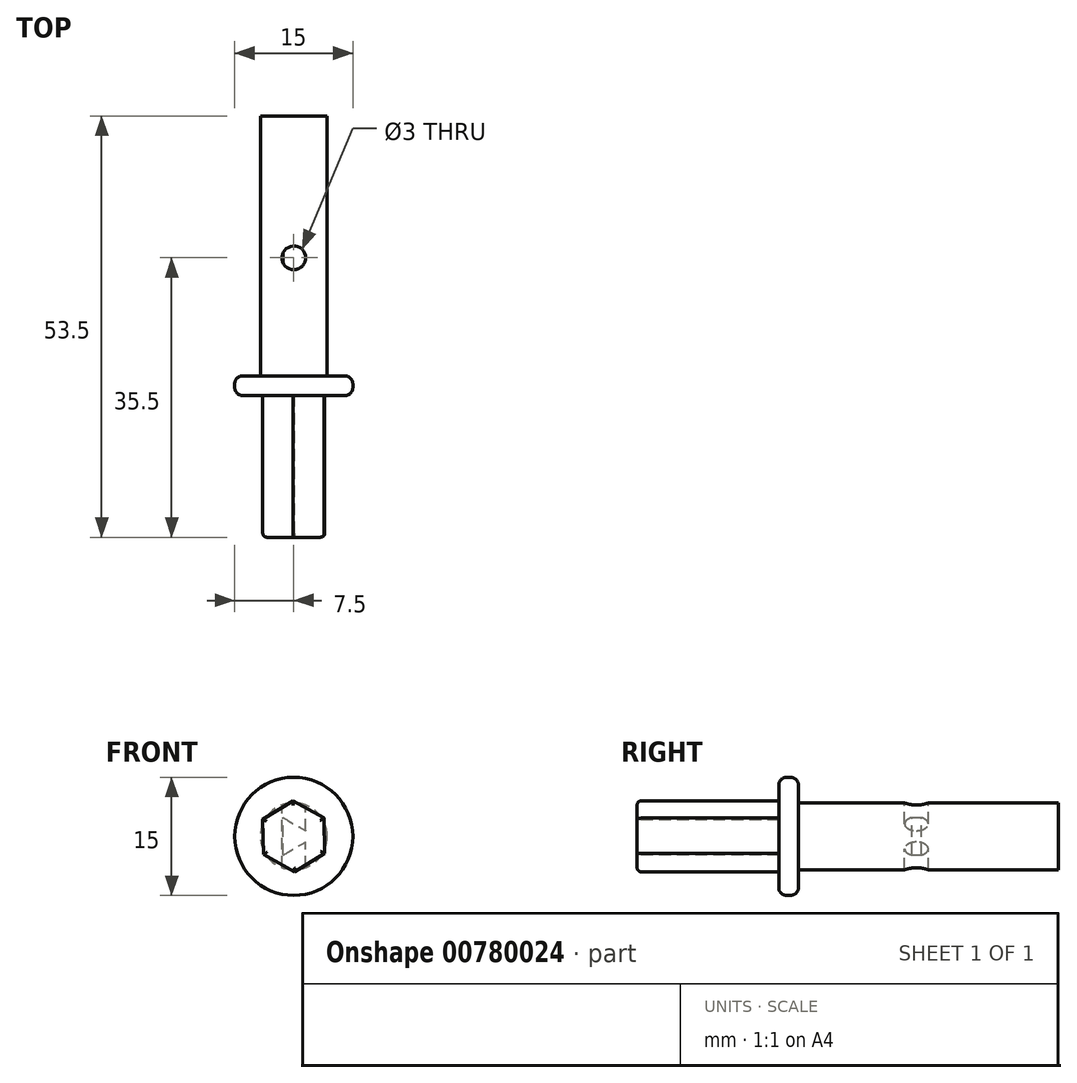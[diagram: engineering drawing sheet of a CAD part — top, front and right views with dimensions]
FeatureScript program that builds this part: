
annotation { "Feature Type Name" : "Feature", "Feature Type Description" : "" }
export const myFeature = defineFeature(function(context is Context, id is Id, definition is map)
    precondition{}
    {
        {
            var Q0;
            Q0=qCreatedBy(makeId("Front.planeOp"),FACE);
            var sketch = newSketch(context, id + "F0", { "sketchPlane" : qUnion([Q0])});
            skCircle(sketch, "E0", {"center": v(0, 0) * mm, "radius": 4.25 * mm});
            skCircle(sketch, "E1.0", {"center": v(0, 0) * mm, "radius": 2.75 * mm, "construction": true});
            skLineSegment(sketch, "E2.0", {"start": v(2.75, 0) * mm, "end": v(-1.38, -2.38) * mm});
            skLineSegment(sketch, "E2.1", {"start": v(-1.37, -2.38) * mm, "end": v(-1.37, 2.38) * mm});
            skLineSegment(sketch, "E2.2", {"start": v(-1.37, 2.38) * mm, "end": v(2.75, 0) * mm});
            skSolve(sketch);
        }
        {
            var Q0;
            Q0=makeQuery(id+"F0.imprint","IMPRINT",FACE,{"disambiguationData":[TD([[makeQuery(id+"F0.imprint","IMPRINT",EDGE,{"derivedFrom":sQuery(id+"F0.wireOp",EDGE,"E0")}),1.0]])]});
            var Q1;
            Q1=makeQuery(id+"F0.imprint","IMPRINT",FACE,{"disambiguationData":[TD([[makeQuery(id+"F0.imprint","IMPRINT",EDGE,{"derivedFrom":sQuery(id+"F0.wireOp",EDGE,"E2.0")}),-1.0]])]});
            extrude(context, id + "F1", {"entities" : qUnion([Q0, Q1]), "depth" : 33 * mm});
        }
        {
            var Q0;
            Q0=makeQuery(id+"F0.imprint","IMPRINT",FACE,{"disambiguationData":[TD([[makeQuery(id+"F0.imprint","IMPRINT",EDGE,{"derivedFrom":sQuery(id+"F0.wireOp",EDGE,"E2.0")}),-1.0]])]});
            extrude(context, id + "F2", {"entities" : qUnion([Q0]), "operationType" : NewBodyOperationType.REMOVE, "depth" : 6 * mm});
        }
        {
            var Q0;
            Q0=makeQuery(id+"F1.opExtrude","CAP_FACE",FACE,{"disambiguationData":[OSD([sQuery(id+"F0.wireOp",EDGE,"E0")])],"isStart":false});
            var sketch = newSketch(context, id + "F3", { "sketchPlane" : qUnion([Q0])});
            skCircle(sketch, "E3", {"center": v(0, 0) * mm, "radius": 7.5 * mm});
            skSolve(sketch);
        }
        {
            var Q0;
            Q0=makeQuery(id+"F3.imprint","IMPRINT",FACE,{"disambiguationData":[TD([[makeQuery(id+"F3.imprint","IMPRINT",EDGE,{"derivedFrom":sQuery(id+"F3.wireOp",EDGE,"E3")}),1.0]])]});
            var Q1;
            Q1=makeQuery(id+"F3.imprint","IMPRINT",FACE,{"disambiguationData":[TD([[makeQuery(id+"F3.imprint","IMPRINT",EDGE,{"derivedFrom":makeQuery(id+"F1.opExtrude","CAP_EDGE",EDGE,{"disambiguationData":[OSD([sQuery(id+"F0.wireOp",EDGE,"E0")])],"isStart":false})}),1.0]])]});
            extrude(context, id + "F4", {"entities" : qUnion([Q0, Q1]), "operationType" : NewBodyOperationType.ADD, "depth" : 2.5 * mm});
        }
        {
            var Q0;
            Q0=makeQuery(id+"F4.opExtrude","CAP_FACE",FACE,{"disambiguationData":[OSD([sQuery(id+"F3.wireOp",EDGE,"E3")])],"isStart":false});
            var sketch = newSketch(context, id + "F5", { "sketchPlane" : qUnion([Q0])});
            skCircle(sketch, "E4", {"center": v(0, 0) * mm, "radius": 4.5 * mm, "construction": true});
            skLineSegment(sketch, "E5.0", {"start": v(3.93, -2.18) * mm, "end": v(0.08, -4.5) * mm});
            skLineSegment(sketch, "E5.1", {"start": v(0.08, -4.5) * mm, "end": v(-3.86, -2.32) * mm});
            skLineSegment(sketch, "E5.2", {"start": v(-3.86, -2.32) * mm, "end": v(-3.93, 2.18) * mm});
            skLineSegment(sketch, "E5.3", {"start": v(-3.93, 2.18) * mm, "end": v(-0.08, 4.5) * mm});
            skLineSegment(sketch, "E5.4", {"start": v(-0.08, 4.5) * mm, "end": v(3.86, 2.32) * mm});
            skLineSegment(sketch, "E5.5", {"start": v(3.86, 2.32) * mm, "end": v(3.93, -2.18) * mm});
            skSolve(sketch);
        }
        {
            var Q0;
            Q0=makeQuery(id+"F5.imprint","IMPRINT",FACE,{"disambiguationData":[TD([[makeQuery(id+"F5.imprint","IMPRINT",EDGE,{"derivedFrom":sQuery(id+"F5.wireOp",EDGE,"E5.0")}),-1.0]])]});
            extrude(context, id + "F6", {"entities" : qUnion([Q0]), "operationType" : NewBodyOperationType.ADD, "depth" : 18 * mm});
        }
        {
            var Q0;
            Q0=makeQuery(id+"F6.opExtrude","CAP_EDGE",EDGE,{"disambiguationData":[OSD([sQuery(id+"F5.wireOp",EDGE,"E5.0")])],"isStart":false});
            var Q1;
            Q1=makeQuery(id+"F6.opExtrude","CAP_EDGE",EDGE,{"disambiguationData":[OSD([sQuery(id+"F5.wireOp",EDGE,"E5.1")])],"isStart":false});
            var Q2;
            Q2=makeQuery(id+"F6.opExtrude","CAP_EDGE",EDGE,{"disambiguationData":[OSD([sQuery(id+"F5.wireOp",EDGE,"E5.2")])],"isStart":false});
            var Q3;
            Q3=makeQuery(id+"F6.opExtrude","CAP_EDGE",EDGE,{"disambiguationData":[OSD([sQuery(id+"F5.wireOp",EDGE,"E5.3")])],"isStart":false});
            var Q4;
            Q4=makeQuery(id+"F6.opExtrude","CAP_EDGE",EDGE,{"disambiguationData":[OSD([sQuery(id+"F5.wireOp",EDGE,"E5.4")])],"isStart":false});
            var Q5;
            Q5=makeQuery(id+"F6.opExtrude","CAP_EDGE",EDGE,{"disambiguationData":[OSD([sQuery(id+"F5.wireOp",EDGE,"E5.5")])],"isStart":false});
            fillet(context, id + "F7", {"entities" : qUnion([Q0, Q1, Q2, Q3, Q4, Q5]), "radius" : .5 * mm, "tangentPropagation" : true, "allowEdgeOverflow" : false});
        }
        {
            var Q0;
            Q0=makeQuery(id+"F4.opExtrude","CAP_EDGE",EDGE,{"disambiguationData":[OSD([sQuery(id+"F3.wireOp",EDGE,"E3")])],"isStart":false});
            var Q1;
            Q1=makeQuery(id+"F4.opExtrude","CAP_EDGE",EDGE,{"disambiguationData":[OSD([sQuery(id+"F3.wireOp",EDGE,"E3")])],"isStart":true});
            fillet(context, id + "F8", {"entities" : qUnion([Q0, Q1]), "radius" : 1 * mm, "tangentPropagation" : true, "allowEdgeOverflow" : false});
        }
        {
            var Q0;
            Q0=qCreatedBy(makeId("Top.planeOp"),FACE);
            cPlane(context, id + "F9", {"entities" : qUnion([Q0]), "cplaneType" : CPlaneType.OFFSET, "offset" : 25 * mm, "width" : 150 * mm, "height" : 150 * mm});
        }
        {
            var Q0;
            Q0=qCreatedBy(id+"F9.planeOp",FACE);
            var sketch = newSketch(context, id + "F10", { "sketchPlane" : qUnion([Q0])});
            skCircle(sketch, "E6", {"center": v(0, -18) * mm, "radius": 1.5 * mm});
            skLineSegment(sketch, "E7", {"start": v(0, 0) * mm, "end": v(0, -18) * mm, "construction": true});
            skSolve(sketch);
        }
        {
            var Q0;
            Q0=makeQuery(id+"F10.imprint","IMPRINT",FACE,{"disambiguationData":[TD([[makeQuery(id+"F10.imprint","IMPRINT",EDGE,{"derivedFrom":sQuery(id+"F10.wireOp",EDGE,"E6")}),1.0]])]});
            extrude(context, id + "F11", {"entities" : qUnion([Q0]), "operationType" : NewBodyOperationType.REMOVE, "oppositeDirection" : true, "depth" : 40 * mm});
        }
        {
            var Q0;
            Q0=makeQuery(id+"F0.imprint","IMPRINT",FACE,{"disambiguationData":[TD([[makeQuery(id+"F0.imprint","IMPRINT",EDGE,{"derivedFrom":sQuery(id+"F0.wireOp",EDGE,"E2.0")}),-1.0]])]});
            extrude(context, id + "F12", {"entities" : qUnion([Q0]), "operationType" : NewBodyOperationType.ADD, "depth" : 25 * mm, "offsetDistance" : 25 * mm});
        }
    });
